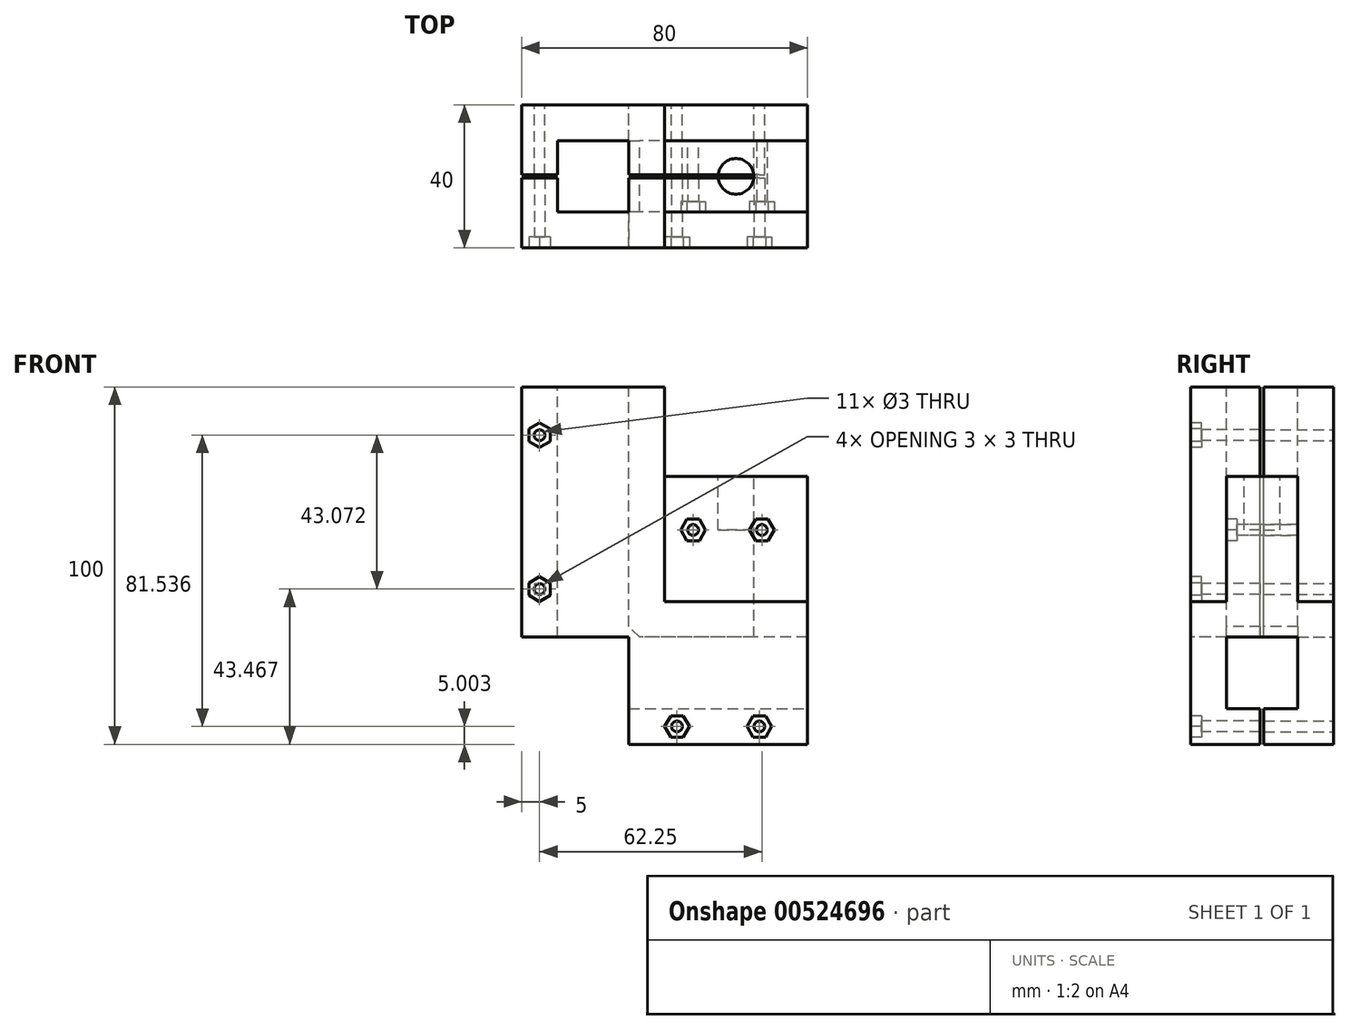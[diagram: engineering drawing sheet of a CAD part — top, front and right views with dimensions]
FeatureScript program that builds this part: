
annotation { "Feature Type Name" : "Feature", "Feature Type Description" : "" }
export const myFeature = defineFeature(function(context is Context, id is Id, definition is map)
    precondition{}
    {
        {
            var Q0;
            Q0=qCreatedBy(makeId("Front.planeOp"),FACE);
            var sketch = newSketch(context, id + "F0", { "sketchPlane" : qUnion([Q0])});
            skLineSegment(sketch, "E0", {"start": v(-50, 89.2) * mm, "end": v(-50, 19.2) * mm});
            skLineSegment(sketch, "E1", {"start": v(-50, 19.2) * mm, "end": v(0, 19.2) * mm});
            skLineSegment(sketch, "E2", {"start": v(0, 19.2) * mm, "end": v(0, 64.2) * mm});
            skLineSegment(sketch, "E3", {"start": v(0, 64.2) * mm, "end": v(-40, 64.2) * mm});
            skLineSegment(sketch, "E4", {"start": v(-40, 64.2) * mm, "end": v(-40, 89.2) * mm});
            skLineSegment(sketch, "E5", {"start": v(-40, 89.2) * mm, "end": v(-50, 89.2) * mm});
            skSolve(sketch);
        }
        {
            var Q0;
            Q0=qSketchRegion(id+"F0",true);
            extrude(context, id + "F1", {"entities" : qUnion([Q0]), "depth" : 20 * mm, "offsetDistance" : 25 * mm});
        }
        {
            var Q0;
            Q0=makeQuery(id+"F1.opExtrude","CAP_FACE",FACE,{"disambiguationData":[OSD([sQuery(id+"F0.wireOp",EDGE,"E0"),sQuery(id+"F0.wireOp",EDGE,"E1"),sQuery(id+"F0.wireOp",EDGE,"E2"),sQuery(id+"F0.wireOp",EDGE,"E3"),sQuery(id+"F0.wireOp",EDGE,"E4"),sQuery(id+"F0.wireOp",EDGE,"E5")])],"isStart":false});
            var sketch = newSketch(context, id + "F2", { "sketchPlane" : qUnion([Q0])});
            skLineSegment(sketch, "E6", {"start": v(-50, 29.2) * mm, "end": v(0, 29.2) * mm});
            skSolve(sketch);
        }
        {
            var Q0;
            {var subQ0=sQuery(id+"F2.wireOp",EDGE,"E6");Q0=makeQuery(id+"F2.imprint","IMPRINT",FACE,{"disambiguationData":[TD([[makeQuery(id+"F2.imprint","IMPRINT",EDGE,{"derivedFrom":subQ0}),-1.0]])]});}
            extrude(context, id + "F3", {"entities" : qUnion([Q0]), "operationType" : NewBodyOperationType.ADD, "depth" : 10 * mm, "offsetDistance" : 25 * mm});
        }
        {
            var Q0;
            Q0=makeQuery(id+"F1.opExtrude","CAP_FACE",FACE,{"disambiguationData":[OSD([sQuery(id+"F0.wireOp",EDGE,"E0"),sQuery(id+"F0.wireOp",EDGE,"E1"),sQuery(id+"F0.wireOp",EDGE,"E2"),sQuery(id+"F0.wireOp",EDGE,"E3"),sQuery(id+"F0.wireOp",EDGE,"E4"),sQuery(id+"F0.wireOp",EDGE,"E5")])],"isStart":true});
            var sketch = newSketch(context, id + "F4", { "sketchPlane" : qUnion([Q0])});
            skLineSegment(sketch, "E7", {"start": v(0, 29.2) * mm, "end": v(50, 29.2) * mm});
            skSolve(sketch);
        }
        {
            var Q0;
            {var subQ0=sQuery(id+"F4.wireOp",EDGE,"E7");Q0=makeQuery(id+"F4.imprint","IMPRINT",FACE,{"disambiguationData":[TD([[makeQuery(id+"F4.imprint","IMPRINT",EDGE,{"derivedFrom":subQ0}),-1.0]])]});}
            extrude(context, id + "F5", {"entities" : qUnion([Q0]), "operationType" : NewBodyOperationType.ADD, "depth" : 10 * mm, "offsetDistance" : 25 * mm});
        }
        {
            var Q0;
            {var subQ0=sQuery(id+"F0.wireOp",EDGE,"E1");Q0=makeQuery(id+"F5.boolean.opBoolean","MERGE",FACE,{"derivedFrom":[makeQuery(id+"F3.boolean.opBoolean","MERGE",FACE,{"derivedFrom":[makeQuery(id+"F1.opExtrude","SWEPT_FACE",FACE,{"disambiguationData":[OSD([subQ0])]}),makeQuery(id+"F3.opExtrude","SWEPT_FACE",FACE,{"disambiguationData":[OSD([subQ0])]})]}),makeQuery(id+"F5.opExtrude","SWEPT_FACE",FACE,{"disambiguationData":[OSD([subQ0])]})]});}
            var sketch = newSketch(context, id + "F6", { "sketchPlane" : qUnion([Q0])});
            skLineSegment(sketch, "E8", {"start": v(0, 20) * mm, "end": v(-50, 20) * mm});
            skLineSegment(sketch, "E9", {"start": v(0, 0) * mm, "end": v(-50, 0) * mm});
            skSolve(sketch);
        }
        {
            var Q0;
            {var subQ0=sQuery(id+"F6.wireOp",EDGE,"E8");Q0=makeQuery(id+"F6.imprint","IMPRINT",FACE,{"disambiguationData":[TD([[makeQuery(id+"F6.imprint","IMPRINT",EDGE,{"derivedFrom":subQ0}),-1.0]])]});}
            var Q1;
            {var subQ0=sQuery(id+"F6.wireOp",EDGE,"E9");Q1=makeQuery(id+"F6.imprint","IMPRINT",FACE,{"disambiguationData":[TD([[makeQuery(id+"F6.imprint","IMPRINT",EDGE,{"derivedFrom":subQ0}),1.0]])]});}
            extrude(context, id + "F7", {"entities" : qUnion([Q0, Q1]), "operationType" : NewBodyOperationType.ADD, "depth" : 30 * mm, "offsetDistance" : 25 * mm});
        }
        {
            var Q0;
            Q0=makeQuery(id+"F5.opExtrude","SWEPT_FACE",FACE,{"disambiguationData":[OSD([sQuery(id+"F4.wireOp",EDGE,"E7")])]});
            var sketch = newSketch(context, id + "F8", { "sketchPlane" : qUnion([Q0])});
            skLineSegment(sketch, "E10", {"start": v(-30, -25) * mm, "end": v(-28.27, -28) * mm});
            skLineSegment(sketch, "E11", {"start": v(-28.27, -28) * mm, "end": v(-24.8, -28) * mm});
            skLineSegment(sketch, "E12", {"start": v(-24.8, -28) * mm, "end": v(-23.07, -25) * mm});
            skLineSegment(sketch, "E13", {"start": v(-23.07, -25) * mm, "end": v(-24.8, -22) * mm});
            skLineSegment(sketch, "E14", {"start": v(-24.8, -22) * mm, "end": v(-28.27, -22) * mm});
            skLineSegment(sketch, "E15", {"start": v(-28.27, -22) * mm, "end": v(-30, -25) * mm});
            skCircle(sketch, "E16", {"center": v(-26.54, -25) * mm, "radius": 1.5 * mm});
            skLineSegment(sketch, "E17", {"start": v(-16.93, -25) * mm, "end": v(-15.2, -28) * mm});
            skLineSegment(sketch, "E18", {"start": v(-15.2, -28) * mm, "end": v(-11.73, -28) * mm});
            skLineSegment(sketch, "E19", {"start": v(-11.73, -28) * mm, "end": v(-10, -25) * mm});
            skLineSegment(sketch, "E20", {"start": v(-10, -25) * mm, "end": v(-11.73, -22) * mm});
            skLineSegment(sketch, "E21", {"start": v(-11.73, -22) * mm, "end": v(-15.2, -22) * mm});
            skLineSegment(sketch, "E22", {"start": v(-15.2, -22) * mm, "end": v(-16.93, -25) * mm});
            skCircle(sketch, "E23", {"center": v(-13.46, -25) * mm, "radius": 1.5 * mm});
            skLineSegment(sketch, "E24", {"start": v(-70, 5) * mm, "end": v(-68.27, 2) * mm});
            skLineSegment(sketch, "E25", {"start": v(-68.27, 2) * mm, "end": v(-64.8, 2) * mm});
            skLineSegment(sketch, "E26", {"start": v(-64.8, 2) * mm, "end": v(-63.07, 5) * mm});
            skLineSegment(sketch, "E27", {"start": v(-63.07, 5) * mm, "end": v(-64.8, 8) * mm});
            skLineSegment(sketch, "E28", {"start": v(-64.8, 8) * mm, "end": v(-68.27, 8) * mm});
            skLineSegment(sketch, "E29", {"start": v(-68.27, 8) * mm, "end": v(-70, 5) * mm});
            skCircle(sketch, "E30", {"center": v(-66.54, 5) * mm, "radius": 1.5 * mm});
            skLineSegment(sketch, "E31", {"start": v(-16.93, 5) * mm, "end": v(-15.2, 2) * mm});
            skLineSegment(sketch, "E32", {"start": v(-15.2, 2) * mm, "end": v(-11.73, 2) * mm});
            skLineSegment(sketch, "E33", {"start": v(-11.73, 2) * mm, "end": v(-10, 5) * mm});
            skLineSegment(sketch, "E34", {"start": v(-10, 5) * mm, "end": v(-11.73, 8) * mm});
            skLineSegment(sketch, "E35", {"start": v(-11.73, 8) * mm, "end": v(-15.2, 8) * mm});
            skLineSegment(sketch, "E36", {"start": v(-15.2, 8) * mm, "end": v(-16.93, 5) * mm});
            skCircle(sketch, "E37", {"center": v(-13.46, 5) * mm, "radius": 1.5 * mm});
            skLineSegment(sketch, "E38", {"start": v(-40, 0) * mm, "end": v(-40, 10) * mm});
            skLineSegment(sketch, "E39.bottom", {"start": v(-40, -20) * mm, "end": v(-50, -20) * mm});
            skLineSegment(sketch, "E39.top", {"start": v(-40, -30) * mm, "end": v(-50, -30) * mm});
            skLineSegment(sketch, "E39.left", {"start": v(-40, -20) * mm, "end": v(-40, -30) * mm});
            skLineSegment(sketch, "E39.right", {"start": v(-50, -20) * mm, "end": v(-50, -30) * mm});
            skSolve(sketch);
        }
        {
            var Q0;
            {var subQ0=sQuery(id+"F8.wireOp",EDGE,"E38");Q0=makeQuery(id+"F8.imprint","IMPRINT",FACE,{"disambiguationData":[TD([[makeQuery(id+"F8.imprint","IMPRINT",EDGE,{"derivedFrom":subQ0}),1.0]])]});}
            var Q1;
            Q1=makeQuery(id+"F8.imprint","IMPRINT",FACE,{"disambiguationData":[TD([[makeQuery(id+"F8.imprint","IMPRINT",EDGE,{"derivedFrom":sQuery(id+"F8.wireOp",EDGE,"E39.bottom")}),1.0]])]});
            extrude(context, id + "F9", {"entities" : qUnion([Q0, Q1]), "operationType" : NewBodyOperationType.ADD, "depth" : 60 * mm, "offsetDistance" : 25 * mm});
        }
        {
            var Q0;
            {var subQ0=sQuery(id+"F0.wireOp",EDGE,"E0");var subQ1=sQuery(id+"F0.wireOp",EDGE,"E1");var subQ2=makeQuery(id+"F5.boolean.opBoolean","MERGE",EDGE,{"derivedFrom":[makeQuery(id+"F3.boolean.opBoolean","MERGE",EDGE,{"derivedFrom":[makeQuery(id+"F1.opExtrude","SWEPT_EDGE",EDGE,{"disambiguationData":[OSD([subQ0,subQ1])]}),makeQuery(id+"F3.opExtrude","SWEPT_EDGE",EDGE,{"disambiguationData":[OSD([subQ0,subQ1])]})]}),makeQuery(id+"F5.opExtrude","SWEPT_EDGE",EDGE,{"disambiguationData":[OSD([subQ0,subQ1])]})]});Q0=makeQuery(id+"F9.boolean.opBoolean","MERGE",FACE,{"derivedFrom":[makeQuery(id+"F7.boolean.opBoolean","MERGE",FACE,{"derivedFrom":[makeQuery(id+"F5.boolean.opBoolean","MERGE",FACE,{"derivedFrom":[makeQuery(id+"F3.boolean.opBoolean","MERGE",FACE,{"derivedFrom":[makeQuery(id+"F1.opExtrude","SWEPT_FACE",FACE,{"disambiguationData":[OSD([subQ0])]}),makeQuery(id+"F3.opExtrude","SWEPT_FACE",FACE,{"disambiguationData":[OSD([subQ0])]})]}),makeQuery(id+"F5.opExtrude","SWEPT_FACE",FACE,{"disambiguationData":[OSD([subQ0])]})]}),makeQuery(id+"F7.opExtrude","SWEPT_FACE",FACE,{"disambiguationData":[OSD([subQ0,subQ1]),TDD([makeQuery(id+"F6.imprint","IMPRINT",EDGE,{"disambiguationData":[TD([[makeQuery(id+"F6.imprint","INTERSECT",VERTEX,{"derivedFrom":[makeQuery(id+"F3.opExtrude","CAP_EDGE",EDGE,{"disambiguationData":[OSD([subQ1])],"isStart":false}),subQ2]}),-1.0]])],"derivedFrom":subQ2})])]}),makeQuery(id+"F7.opExtrude","SWEPT_FACE",FACE,{"disambiguationData":[OSD([subQ0,subQ1]),TDD([makeQuery(id+"F6.imprint","IMPRINT",EDGE,{"disambiguationData":[TD([[makeQuery(id+"F6.imprint","INTERSECT",VERTEX,{"derivedFrom":[makeQuery(id+"F5.opExtrude","CAP_EDGE",EDGE,{"disambiguationData":[OSD([subQ1])],"isStart":false}),subQ2]}),1.0]])],"derivedFrom":subQ2})])]})]}),makeQuery(id+"F9.opExtrude","SWEPT_FACE",FACE,{"disambiguationData":[OSD([sQuery(id+"F8.wireOp",EDGE,"E39.right")])]}),makeQuery(id+"F9.opExtrude","SWEPT_FACE",FACE,{"disambiguationData":[OSD([subQ0,sQuery(id+"F4.wireOp",EDGE,"E7")])]})]});}
            var sketch = newSketch(context, id + "F10", { "sketchPlane" : qUnion([Q0])});
            skLineSegment(sketch, "E40", {"start": v(20, 19.2) * mm, "end": v(20, 89.2) * mm});
            skLineSegment(sketch, "E41", {"start": v(0, 19.2) * mm, "end": v(0, 89.2) * mm});
            skLineSegment(sketch, "E42", {"start": v(20, 19.2) * mm, "end": v(30, 19.2) * mm});
            skLineSegment(sketch, "E43", {"start": v(0, 19.2) * mm, "end": v(-10, 19.2) * mm});
            skSolve(sketch);
        }
        {
            var Q0;
            {var subQ0=sQuery(id+"F10.wireOp",EDGE,"E40");Q0=makeQuery(id+"F10.imprint","IMPRINT",FACE,{"disambiguationData":[TD([[makeQuery(id+"F10.imprint","IMPRINT",EDGE,{"derivedFrom":subQ0}),-1.0]])]});}
            var Q1;
            {var subQ0=sQuery(id+"F10.wireOp",EDGE,"E41");Q1=makeQuery(id+"F10.imprint","IMPRINT",FACE,{"disambiguationData":[TD([[makeQuery(id+"F10.imprint","IMPRINT",EDGE,{"derivedFrom":subQ0}),1.0]])]});}
            extrude(context, id + "F11", {"entities" : qUnion([Q0, Q1]), "operationType" : NewBodyOperationType.ADD, "depth" : 30 * mm, "offsetDistance" : 25 * mm});
        }
        {
            var Q0;
            Q0=makeQuery(id+"F1.opExtrude","SWEPT_FACE",FACE,{"disambiguationData":[OSD([sQuery(id+"F0.wireOp",EDGE,"E3")])]});
            var sketch = newSketch(context, id + "F12", { "sketchPlane" : qUnion([Q0])});
            skCircle(sketch, "E44", {"center": v(-20, -10) * mm, "radius": 5 * mm});
            skSolve(sketch);
        }
        {
            var Q0;
            Q0=makeQuery(id+"F12.imprint","IMPRINT",FACE,{"disambiguationData":[TD([[makeQuery(id+"F12.imprint","IMPRINT",EDGE,{"derivedFrom":sQuery(id+"F12.wireOp",EDGE,"E44")}),1.0]])]});
            extrude(context, id + "F13", {"entities" : qUnion([Q0]), "operationType" : NewBodyOperationType.REMOVE, "oppositeDirection" : true, "depth" : 15 * mm, "offsetDistance" : 25 * mm});
        }
        {
            var Q0;
            {var subQ0=sQuery(id+"F8.wireOp",EDGE,"E39.right");var subQ1=sQuery(id+"F8.wireOp",EDGE,"E39.top");var subQ3=sQuery(id+"F0.wireOp",EDGE,"E0");var subQ5=sQuery(id+"F4.wireOp",EDGE,"E7");var subQ6=sQuery(id+"F0.wireOp",EDGE,"E5");var subQ7=makeQuery(id+"F9.boolean.opBoolean","MERGE",EDGE,{"derivedFrom":[makeQuery(id+"F1.opExtrude","SWEPT_EDGE",EDGE,{"disambiguationData":[OSD([subQ3,subQ6])]}),makeQuery(id+"F9.opExtrude","CAP_EDGE",EDGE,{"disambiguationData":[OSD([subQ0])],"isStart":false}),makeQuery(id+"F9.opExtrude","CAP_EDGE",EDGE,{"disambiguationData":[OSD([subQ3,subQ5])],"isStart":false})]});Q0=makeQuery(id+"F11.boolean.opBoolean","MERGE",FACE,{"derivedFrom":[makeQuery(id+"F9.boolean.opBoolean","MERGE",FACE,{"derivedFrom":[makeQuery(id+"F1.opExtrude","SWEPT_FACE",FACE,{"disambiguationData":[OSD([subQ6])]}),makeQuery(id+"F9.opExtrude","CAP_FACE",FACE,{"disambiguationData":[OSD([subQ3,subQ5,sQuery(id+"F8.wireOp",EDGE,"E38")])],"isStart":false}),makeQuery(id+"F9.opExtrude","CAP_FACE",FACE,{"disambiguationData":[OSD([sQuery(id+"F8.wireOp",EDGE,"E39.bottom"),subQ1,sQuery(id+"F8.wireOp",EDGE,"E39.left"),subQ0])],"isStart":false})]}),makeQuery(id+"F11.opExtrude","SWEPT_FACE",FACE,{"disambiguationData":[OSD([subQ3,subQ6,subQ5,subQ0]),TDD([makeQuery(id+"F10.imprint","IMPRINT",EDGE,{"disambiguationData":[TD([[makeQuery(id+"F10.imprint","INTERSECT",VERTEX,{"derivedFrom":[subQ7,sQuery(id+"F10.wireOp",EDGE,"E41")]}),-1.0]])],"derivedFrom":subQ7})])]}),makeQuery(id+"F11.opExtrude","SWEPT_FACE",FACE,{"disambiguationData":[OSD([subQ3,subQ6,subQ5,subQ0]),TDD([makeQuery(id+"F10.imprint","IMPRINT",EDGE,{"disambiguationData":[TD([[makeQuery(id+"F10.imprint","INTERSECT",VERTEX,{"derivedFrom":[subQ7,sQuery(id+"F10.wireOp",EDGE,"E40")]}),1.0]])],"derivedFrom":subQ7})])]})]});}
            var sketch = newSketch(context, id + "F14", { "sketchPlane" : qUnion([Q0])});
            skLineSegment(sketch, "E45", {"start": v(-40, -10) * mm, "end": v(-40, -9.5) * mm});
            skLineSegment(sketch, "E46", {"start": v(-40, -10) * mm, "end": v(-40, -10.5) * mm});
            skLineSegment(sketch, "E47", {"start": v(-40, -10.5) * mm, "end": v(-50, -10.5) * mm});
            skLineSegment(sketch, "E48", {"start": v(-40, -9.5) * mm, "end": v(-50, -9.5) * mm});
            skSolve(sketch);
        }
        {
            var Q0;
            Q0=makeQuery(id+"F1.opExtrude","SWEPT_FACE",FACE,{"disambiguationData":[OSD([sQuery(id+"F0.wireOp",EDGE,"E3")])]});
            var sketch = newSketch(context, id + "F15", { "sketchPlane" : qUnion([Q0])});
            skLineSegment(sketch, "E49", {"start": v(-40, 54.2) * mm, "end": v(-40, -10.5) * mm});
            skLineSegment(sketch, "E50", {"start": v(-40, -10.5) * mm, "end": v(0, -10.5) * mm});
            skLineSegment(sketch, "E51", {"start": v(-40, -9.5) * mm, "end": v(0, -9.5) * mm});
            skSolve(sketch);
        }
        {
            var Q0;
            {var subQ0=sQuery(id+"F15.wireOp",EDGE,"E50");var subQ3=makeQuery(id+"F13.boolean.opBoolean","COPY",EDGE,{"derivedFrom":makeQuery(id+"F13.opExtrude","CAP_EDGE",EDGE,{"disambiguationData":[OSD([sQuery(id+"F12.wireOp",EDGE,"E44")])],"isStart":true})});var subQ4=makeQuery(id+"F15.imprint","INTERSECT",VERTEX,{"disambiguationData":[OD(1.0)],"derivedFrom":[subQ3,subQ0]});Q0=makeQuery(id+"F15.imprint","IMPRINT",FACE,{"disambiguationData":[TD([[makeQuery(id+"F15.imprint","IMPRINT",EDGE,{"disambiguationData":[TD([[subQ4,-1.0]])],"derivedFrom":subQ3}),-1.0]])]});}
            var Q1;
            Q1=makeQuery(id+"F14.imprint","IMPRINT",FACE,{"disambiguationData":[TD([[makeQuery(id+"F14.imprint","IMPRINT",EDGE,{"derivedFrom":sQuery(id+"F14.wireOp",EDGE,"E45")}),1.0]])]});
            var Q2;
            {var subQ0=sQuery(id+"F15.wireOp",EDGE,"E50");var subQ1=makeQuery(id+"F13.boolean.opBoolean","COPY",EDGE,{"derivedFrom":makeQuery(id+"F13.opExtrude","CAP_EDGE",EDGE,{"disambiguationData":[OSD([sQuery(id+"F12.wireOp",EDGE,"E44")])],"isStart":true})});var subQ2=makeQuery(id+"F15.imprint","INTERSECT",VERTEX,{"disambiguationData":[OD(0.0)],"derivedFrom":[subQ1,subQ0]});Q2=makeQuery(id+"F15.imprint","IMPRINT",FACE,{"disambiguationData":[TD([[makeQuery(id+"F15.imprint","IMPRINT",EDGE,{"disambiguationData":[TD([[subQ2,-1.0]])],"derivedFrom":subQ0}),1.0]])]});}
            var Q3;
            {var subQ1=sQuery(id+"F15.wireOp",EDGE,"E49");var subQ3=sQuery(id+"F15.wireOp",EDGE,"E51");var subQ4=makeQuery(id+"F15.imprint","INTERSECT",VERTEX,{"derivedFrom":[subQ1,subQ3]});Q3=makeQuery(id+"F15.imprint","IMPRINT",FACE,{"disambiguationData":[TD([[makeQuery(id+"F15.imprint","IMPRINT",EDGE,{"disambiguationData":[TD([[subQ4,-1.0]])],"derivedFrom":subQ3}),-1.0]])]});}
            extrude(context, id + "F16", {"entities" : qUnion([Q0, Q1, Q2, Q3]), "operationType" : NewBodyOperationType.REMOVE, "oppositeDirection" : true, "depth" : 70 * mm, "offsetDistance" : 25 * mm});
        }
        {
            var Q0;
            {var subQ0=sQuery(id+"F0.wireOp",EDGE,"E1");var subQ1=sQuery(id+"F0.wireOp",EDGE,"E0");var subQ2=makeQuery(id+"F5.boolean.opBoolean","MERGE",EDGE,{"derivedFrom":[makeQuery(id+"F3.boolean.opBoolean","MERGE",EDGE,{"derivedFrom":[makeQuery(id+"F1.opExtrude","SWEPT_EDGE",EDGE,{"disambiguationData":[OSD([subQ1,subQ0])]}),makeQuery(id+"F3.opExtrude","SWEPT_EDGE",EDGE,{"disambiguationData":[OSD([subQ1,subQ0])]})]}),makeQuery(id+"F5.opExtrude","SWEPT_EDGE",EDGE,{"disambiguationData":[OSD([subQ1,subQ0])]})]});var subQ3=sQuery(id+"F6.wireOp",EDGE,"E9");Q0=makeQuery(id+"F16.boolean.opBoolean","SPLIT",EDGE,{"disambiguationData":[TD([makeQuery(id+"F7.opExtrude","SWEPT_FACE",FACE,{"disambiguationData":[OSD([subQ3])]})])],"derivedFrom":subQ2});}
            var Q1;
            {var subQ0=sQuery(id+"F0.wireOp",EDGE,"E1");var subQ1=sQuery(id+"F0.wireOp",EDGE,"E0");var subQ2=makeQuery(id+"F5.boolean.opBoolean","MERGE",EDGE,{"derivedFrom":[makeQuery(id+"F3.boolean.opBoolean","MERGE",EDGE,{"derivedFrom":[makeQuery(id+"F1.opExtrude","SWEPT_EDGE",EDGE,{"disambiguationData":[OSD([subQ1,subQ0])]}),makeQuery(id+"F3.opExtrude","SWEPT_EDGE",EDGE,{"disambiguationData":[OSD([subQ1,subQ0])]})]}),makeQuery(id+"F5.opExtrude","SWEPT_EDGE",EDGE,{"disambiguationData":[OSD([subQ1,subQ0])]})]});var subQ3=sQuery(id+"F6.wireOp",EDGE,"E8");Q1=makeQuery(id+"F16.boolean.opBoolean","SPLIT",EDGE,{"disambiguationData":[TD([makeQuery(id+"F7.opExtrude","SWEPT_FACE",FACE,{"disambiguationData":[OSD([subQ3])]})])],"derivedFrom":subQ2});}
            chamfer(context, id + "F17", {"entities" : qUnion([Q0, Q1]), "width" : 3 * mm, "tangentPropagation" : true});
        }
        {
            var Q0;
            Q0=makeQuery(id+"F17.opChamfer","MERGE",FACE,{"derivedFrom":[makeQuery(id+"F7.opExtrude","SWEPT_FACE",FACE,{"disambiguationData":[OSD([sQuery(id+"F6.wireOp",EDGE,"E9")])]}),makeQuery(id+"F11.opExtrude","SWEPT_FACE",FACE,{"disambiguationData":[OSD([sQuery(id+"F10.wireOp",EDGE,"E41")])]})]});
            var sketch = newSketch(context, id + "F18", { "sketchPlane" : qUnion([Q0])});
            skLineSegment(sketch, "E52", {"start": v(-80, 19.2) * mm, "end": v(-70, 19.2) * mm});
            skLineSegment(sketch, "E53", {"start": v(-70, 19.2) * mm, "end": v(-70, 89.2) * mm});
            skLineSegment(sketch, "E54", {"start": v(-50, -10.8) * mm, "end": v(-50, -0.8) * mm});
            skLineSegment(sketch, "E55", {"start": v(-50, -0.8) * mm, "end": v(0, -0.8) * mm});
            skSolve(sketch);
        }
        {
            var Q0;
            Q0=makeQuery(id+"F17.opChamfer","MERGE",FACE,{"derivedFrom":[makeQuery(id+"F7.opExtrude","SWEPT_FACE",FACE,{"disambiguationData":[OSD([sQuery(id+"F6.wireOp",EDGE,"E8")])]}),makeQuery(id+"F11.opExtrude","SWEPT_FACE",FACE,{"disambiguationData":[OSD([sQuery(id+"F10.wireOp",EDGE,"E40")])]})]});
            var sketch = newSketch(context, id + "F19", { "sketchPlane" : qUnion([Q0])});
            skLineSegment(sketch, "E56", {"start": v(80, 19.2) * mm, "end": v(70, 19.2) * mm});
            skLineSegment(sketch, "E57", {"start": v(70, 19.2) * mm, "end": v(70, 89.2) * mm});
            skLineSegment(sketch, "E58", {"start": v(50, -10.8) * mm, "end": v(50, -0.8) * mm});
            skLineSegment(sketch, "E59", {"start": v(50, -0.8) * mm, "end": v(0, -0.8) * mm});
            skSolve(sketch);
        }
        {
            var Q0;
            Q0=makeQuery(id+"F18.imprint","IMPRINT",FACE,{"disambiguationData":[TD([[makeQuery(id+"F18.imprint","IMPRINT",EDGE,{"derivedFrom":sQuery(id+"F18.wireOp",EDGE,"E52")}),1.0]])]});
            var Q1;
            Q1=makeQuery(id+"F18.imprint","IMPRINT",FACE,{"disambiguationData":[TD([[makeQuery(id+"F18.imprint","IMPRINT",EDGE,{"derivedFrom":sQuery(id+"F18.wireOp",EDGE,"E54")}),-1.0]])]});
            extrude(context, id + "F20", {"entities" : qUnion([Q0, Q1]), "operationType" : NewBodyOperationType.ADD, "depth" : 9.5 * mm, "offsetDistance" : 25 * mm});
        }
        {
            var Q0;
            Q0=makeQuery(id+"F19.imprint","IMPRINT",FACE,{"disambiguationData":[TD([[makeQuery(id+"F19.imprint","IMPRINT",EDGE,{"derivedFrom":sQuery(id+"F19.wireOp",EDGE,"E56")}),-1.0]])]});
            var Q1;
            Q1=makeQuery(id+"F19.imprint","IMPRINT",FACE,{"disambiguationData":[TD([[makeQuery(id+"F19.imprint","IMPRINT",EDGE,{"derivedFrom":sQuery(id+"F19.wireOp",EDGE,"E58")}),1.0]])]});
            extrude(context, id + "F21", {"entities" : qUnion([Q0, Q1]), "operationType" : NewBodyOperationType.ADD, "depth" : 9.5 * mm, "offsetDistance" : 25 * mm});
        }
        {
            var Q0;
            {var subQ0=sQuery(id+"F8.wireOp",EDGE,"E39.top");var subQ1=sQuery(id+"F0.wireOp",EDGE,"E1");var subQ2=sQuery(id+"F0.wireOp",EDGE,"E0");Q0=makeQuery(id+"F11.boolean.opBoolean","MERGE",FACE,{"derivedFrom":[makeQuery(id+"F9.boolean.opBoolean","MERGE",FACE,{"derivedFrom":[makeQuery(id+"F7.boolean.opBoolean","MERGE",FACE,{"derivedFrom":[makeQuery(id+"F3.opExtrude","CAP_FACE",FACE,{"disambiguationData":[OSD([subQ2,subQ1,sQuery(id+"F0.wireOp",EDGE,"E2"),sQuery(id+"F2.wireOp",EDGE,"E6")])],"isStart":false}),makeQuery(id+"F7.opExtrude","SWEPT_FACE",FACE,{"disambiguationData":[OSD([subQ1]),TDD([makeQuery(id+"F6.imprint","IMPRINT",EDGE,{"derivedFrom":makeQuery(id+"F3.opExtrude","CAP_EDGE",EDGE,{"disambiguationData":[OSD([subQ1])],"isStart":false})})])]})]}),makeQuery(id+"F9.opExtrude","SWEPT_FACE",FACE,{"disambiguationData":[OSD([subQ0])]})]}),makeQuery(id+"F11.opExtrude","SWEPT_FACE",FACE,{"disambiguationData":[OSD([subQ2,subQ1,subQ0,sQuery(id+"F8.wireOp",EDGE,"E39.right")])]})]});}
            var sketch = newSketch(context, id + "F22", { "sketchPlane" : qUnion([Q0])});
            skLineSegment(sketch, "E60", {"start": v(-75, 79.2) * mm, "end": v(-78, 77.46) * mm});
            skLineSegment(sketch, "E61", {"start": v(-78, 77.46) * mm, "end": v(-78, 74) * mm});
            skLineSegment(sketch, "E62", {"start": v(-78, 74) * mm, "end": v(-75, 72.26) * mm});
            skLineSegment(sketch, "E63", {"start": v(-75, 72.26) * mm, "end": v(-72, 74) * mm});
            skLineSegment(sketch, "E64", {"start": v(-72, 74) * mm, "end": v(-72, 77.46) * mm});
            skLineSegment(sketch, "E65", {"start": v(-72, 77.46) * mm, "end": v(-75, 79.2) * mm});
            skCircle(sketch, "E66", {"center": v(-75, 75.73) * mm, "radius": 1.5 * mm});
            skLineSegment(sketch, "E67", {"start": v(-75, 36.12) * mm, "end": v(-78, 34.39) * mm});
            skLineSegment(sketch, "E68", {"start": v(-78, 34.39) * mm, "end": v(-78, 30.93) * mm});
            skLineSegment(sketch, "E69", {"start": v(-78, 30.93) * mm, "end": v(-75, 29.2) * mm});
            skLineSegment(sketch, "E70", {"start": v(-75, 29.2) * mm, "end": v(-72, 30.93) * mm});
            skLineSegment(sketch, "E71", {"start": v(-72, 30.93) * mm, "end": v(-72, 34.39) * mm});
            skLineSegment(sketch, "E72", {"start": v(-72, 34.39) * mm, "end": v(-75, 36.12) * mm});
            skCircle(sketch, "E73", {"center": v(-75, 32.66) * mm, "radius": 1.5 * mm});
            skLineSegment(sketch, "E74", {"start": v(-40, -5.8) * mm, "end": v(-38.27, -8.8) * mm});
            skLineSegment(sketch, "E75", {"start": v(-38.27, -8.8) * mm, "end": v(-34.8, -8.8) * mm});
            skLineSegment(sketch, "E76", {"start": v(-34.8, -8.8) * mm, "end": v(-33.07, -5.8) * mm});
            skLineSegment(sketch, "E77", {"start": v(-33.07, -5.8) * mm, "end": v(-34.8, -2.8) * mm});
            skLineSegment(sketch, "E78", {"start": v(-34.8, -2.8) * mm, "end": v(-38.27, -2.8) * mm});
            skLineSegment(sketch, "E79", {"start": v(-38.27, -2.8) * mm, "end": v(-40, -5.8) * mm});
            skCircle(sketch, "E80", {"center": v(-36.54, -5.8) * mm, "radius": 1.5 * mm});
            skLineSegment(sketch, "E81", {"start": v(-16.93, -5.8) * mm, "end": v(-15.2, -8.8) * mm});
            skLineSegment(sketch, "E82", {"start": v(-15.2, -8.8) * mm, "end": v(-11.73, -8.8) * mm});
            skLineSegment(sketch, "E83", {"start": v(-11.73, -8.8) * mm, "end": v(-10, -5.8) * mm});
            skLineSegment(sketch, "E84", {"start": v(-10, -5.8) * mm, "end": v(-11.73, -2.8) * mm});
            skLineSegment(sketch, "E85", {"start": v(-11.73, -2.8) * mm, "end": v(-15.2, -2.8) * mm});
            skLineSegment(sketch, "E86", {"start": v(-15.2, -2.8) * mm, "end": v(-16.93, -5.8) * mm});
            skCircle(sketch, "E87", {"center": v(-13.46, -5.8) * mm, "radius": 1.5 * mm});
            skSolve(sketch);
        }
        {
            var Q0;
            Q0=makeQuery(id+"F22.imprint","IMPRINT",FACE,{"disambiguationData":[TD([[makeQuery(id+"F22.imprint","IMPRINT",EDGE,{"derivedFrom":sQuery(id+"F22.wireOp",EDGE,"E60")}),1.0]])]});
            var Q1;
            Q1=makeQuery(id+"F22.imprint","IMPRINT",FACE,{"disambiguationData":[TD([[makeQuery(id+"F22.imprint","IMPRINT",EDGE,{"derivedFrom":sQuery(id+"F22.wireOp",EDGE,"E67")}),1.0]])]});
            var Q2;
            Q2=makeQuery(id+"F22.imprint","IMPRINT",FACE,{"disambiguationData":[TD([[makeQuery(id+"F22.imprint","IMPRINT",EDGE,{"derivedFrom":sQuery(id+"F22.wireOp",EDGE,"E74")}),1.0]])]});
            var Q3;
            Q3=makeQuery(id+"F22.imprint","IMPRINT",FACE,{"disambiguationData":[TD([[makeQuery(id+"F22.imprint","IMPRINT",EDGE,{"derivedFrom":sQuery(id+"F22.wireOp",EDGE,"E81")}),1.0]])]});
            extrude(context, id + "F23", {"entities" : qUnion([Q0, Q1, Q2, Q3]), "operationType" : NewBodyOperationType.REMOVE, "oppositeDirection" : true, "depth" : 3 * mm, "offsetDistance" : 25 * mm});
        }
        {
            var Q0;
            {var subQ0=sQuery(id+"F8.wireOp",EDGE,"E39.top");var subQ1=sQuery(id+"F0.wireOp",EDGE,"E1");var subQ2=sQuery(id+"F0.wireOp",EDGE,"E0");Q0=makeQuery(id+"F23.boolean.opBoolean","SPLIT",FACE,{"disambiguationData":[TD([makeQuery(id+"F23.opExtrude","SWEPT_FACE",FACE,{"disambiguationData":[OSD([sQuery(id+"F22.wireOp",EDGE,"E66")])]})])],"derivedFrom":makeQuery(id+"F11.boolean.opBoolean","MERGE",FACE,{"derivedFrom":[makeQuery(id+"F9.boolean.opBoolean","MERGE",FACE,{"derivedFrom":[makeQuery(id+"F7.boolean.opBoolean","MERGE",FACE,{"derivedFrom":[makeQuery(id+"F3.opExtrude","CAP_FACE",FACE,{"disambiguationData":[OSD([subQ2,subQ1,sQuery(id+"F0.wireOp",EDGE,"E2"),sQuery(id+"F2.wireOp",EDGE,"E6")])],"isStart":false}),makeQuery(id+"F7.opExtrude","SWEPT_FACE",FACE,{"disambiguationData":[OSD([subQ1]),TDD([makeQuery(id+"F6.imprint","IMPRINT",EDGE,{"derivedFrom":makeQuery(id+"F3.opExtrude","CAP_EDGE",EDGE,{"disambiguationData":[OSD([subQ1])],"isStart":false})})])]})]}),makeQuery(id+"F9.opExtrude","SWEPT_FACE",FACE,{"disambiguationData":[OSD([subQ0])]})]}),makeQuery(id+"F11.opExtrude","SWEPT_FACE",FACE,{"disambiguationData":[OSD([subQ2,subQ1,subQ0,sQuery(id+"F8.wireOp",EDGE,"E39.right")])]})]})});}
            var Q1;
            {var subQ0=sQuery(id+"F8.wireOp",EDGE,"E39.top");var subQ1=sQuery(id+"F0.wireOp",EDGE,"E1");var subQ2=sQuery(id+"F0.wireOp",EDGE,"E0");Q1=makeQuery(id+"F23.boolean.opBoolean","SPLIT",FACE,{"disambiguationData":[TD([makeQuery(id+"F23.opExtrude","SWEPT_FACE",FACE,{"disambiguationData":[OSD([sQuery(id+"F22.wireOp",EDGE,"E73")])]})])],"derivedFrom":makeQuery(id+"F11.boolean.opBoolean","MERGE",FACE,{"derivedFrom":[makeQuery(id+"F9.boolean.opBoolean","MERGE",FACE,{"derivedFrom":[makeQuery(id+"F7.boolean.opBoolean","MERGE",FACE,{"derivedFrom":[makeQuery(id+"F3.opExtrude","CAP_FACE",FACE,{"disambiguationData":[OSD([subQ2,subQ1,sQuery(id+"F0.wireOp",EDGE,"E2"),sQuery(id+"F2.wireOp",EDGE,"E6")])],"isStart":false}),makeQuery(id+"F7.opExtrude","SWEPT_FACE",FACE,{"disambiguationData":[OSD([subQ1]),TDD([makeQuery(id+"F6.imprint","IMPRINT",EDGE,{"derivedFrom":makeQuery(id+"F3.opExtrude","CAP_EDGE",EDGE,{"disambiguationData":[OSD([subQ1])],"isStart":false})})])]})]}),makeQuery(id+"F9.opExtrude","SWEPT_FACE",FACE,{"disambiguationData":[OSD([subQ0])]})]}),makeQuery(id+"F11.opExtrude","SWEPT_FACE",FACE,{"disambiguationData":[OSD([subQ2,subQ1,subQ0,sQuery(id+"F8.wireOp",EDGE,"E39.right")])]})]})});}
            var Q2;
            {var subQ0=sQuery(id+"F8.wireOp",EDGE,"E39.top");var subQ1=sQuery(id+"F0.wireOp",EDGE,"E1");var subQ2=sQuery(id+"F0.wireOp",EDGE,"E0");Q2=makeQuery(id+"F23.boolean.opBoolean","SPLIT",FACE,{"disambiguationData":[TD([makeQuery(id+"F23.opExtrude","SWEPT_FACE",FACE,{"disambiguationData":[OSD([sQuery(id+"F22.wireOp",EDGE,"E80")])]})])],"derivedFrom":makeQuery(id+"F11.boolean.opBoolean","MERGE",FACE,{"derivedFrom":[makeQuery(id+"F9.boolean.opBoolean","MERGE",FACE,{"derivedFrom":[makeQuery(id+"F7.boolean.opBoolean","MERGE",FACE,{"derivedFrom":[makeQuery(id+"F3.opExtrude","CAP_FACE",FACE,{"disambiguationData":[OSD([subQ2,subQ1,sQuery(id+"F0.wireOp",EDGE,"E2"),sQuery(id+"F2.wireOp",EDGE,"E6")])],"isStart":false}),makeQuery(id+"F7.opExtrude","SWEPT_FACE",FACE,{"disambiguationData":[OSD([subQ1]),TDD([makeQuery(id+"F6.imprint","IMPRINT",EDGE,{"derivedFrom":makeQuery(id+"F3.opExtrude","CAP_EDGE",EDGE,{"disambiguationData":[OSD([subQ1])],"isStart":false})})])]})]}),makeQuery(id+"F9.opExtrude","SWEPT_FACE",FACE,{"disambiguationData":[OSD([subQ0])]})]}),makeQuery(id+"F11.opExtrude","SWEPT_FACE",FACE,{"disambiguationData":[OSD([subQ2,subQ1,subQ0,sQuery(id+"F8.wireOp",EDGE,"E39.right")])]})]})});}
            var Q3;
            {var subQ0=sQuery(id+"F8.wireOp",EDGE,"E39.top");var subQ1=sQuery(id+"F0.wireOp",EDGE,"E1");var subQ2=sQuery(id+"F0.wireOp",EDGE,"E0");Q3=makeQuery(id+"F23.boolean.opBoolean","SPLIT",FACE,{"disambiguationData":[TD([makeQuery(id+"F23.opExtrude","SWEPT_FACE",FACE,{"disambiguationData":[OSD([sQuery(id+"F22.wireOp",EDGE,"E87")])]})])],"derivedFrom":makeQuery(id+"F11.boolean.opBoolean","MERGE",FACE,{"derivedFrom":[makeQuery(id+"F9.boolean.opBoolean","MERGE",FACE,{"derivedFrom":[makeQuery(id+"F7.boolean.opBoolean","MERGE",FACE,{"derivedFrom":[makeQuery(id+"F3.opExtrude","CAP_FACE",FACE,{"disambiguationData":[OSD([subQ2,subQ1,sQuery(id+"F0.wireOp",EDGE,"E2"),sQuery(id+"F2.wireOp",EDGE,"E6")])],"isStart":false}),makeQuery(id+"F7.opExtrude","SWEPT_FACE",FACE,{"disambiguationData":[OSD([subQ1]),TDD([makeQuery(id+"F6.imprint","IMPRINT",EDGE,{"derivedFrom":makeQuery(id+"F3.opExtrude","CAP_EDGE",EDGE,{"disambiguationData":[OSD([subQ1])],"isStart":false})})])]})]}),makeQuery(id+"F9.opExtrude","SWEPT_FACE",FACE,{"disambiguationData":[OSD([subQ0])]})]}),makeQuery(id+"F11.opExtrude","SWEPT_FACE",FACE,{"disambiguationData":[OSD([subQ2,subQ1,subQ0,sQuery(id+"F8.wireOp",EDGE,"E39.right")])]})]})});}
            extrude(context, id + "F24", {"entities" : qUnion([Q0, Q1, Q2, Q3]), "operationType" : NewBodyOperationType.REMOVE, "oppositeDirection" : true, "depth" : 20 * mm, "offsetDistance" : 25 * mm});
        }
        {
            var Q0;
            {var subQ0=sQuery(id+"F4.wireOp",EDGE,"E7");var subQ1=sQuery(id+"F0.wireOp",EDGE,"E1");var subQ2=sQuery(id+"F0.wireOp",EDGE,"E0");var subQ3=makeQuery(id+"F5.opExtrude","CAP_EDGE",EDGE,{"disambiguationData":[OSD([subQ0])],"isStart":false});Q0=makeQuery(id+"F11.boolean.opBoolean","MERGE",FACE,{"derivedFrom":[makeQuery(id+"F9.boolean.opBoolean","MERGE",FACE,{"derivedFrom":[makeQuery(id+"F7.boolean.opBoolean","MERGE",FACE,{"derivedFrom":[makeQuery(id+"F5.opExtrude","CAP_FACE",FACE,{"disambiguationData":[OSD([subQ2,subQ1,sQuery(id+"F0.wireOp",EDGE,"E2"),subQ0])],"isStart":false}),makeQuery(id+"F7.opExtrude","SWEPT_FACE",FACE,{"disambiguationData":[OSD([subQ1]),TDD([makeQuery(id+"F6.imprint","IMPRINT",EDGE,{"derivedFrom":makeQuery(id+"F5.opExtrude","CAP_EDGE",EDGE,{"disambiguationData":[OSD([subQ1])],"isStart":false})})])]})]}),makeQuery(id+"F9.opExtrude","SWEPT_FACE",FACE,{"disambiguationData":[OSD([subQ0]),TDD([makeQuery(id+"F8.imprint","IMPRINT",EDGE,{"disambiguationData":[TD([[makeQuery(id+"F8.imprint","INTERSECT",VERTEX,{"derivedFrom":[subQ3,sQuery(id+"F8.wireOp",EDGE,"E38")]}),-1.0]])],"derivedFrom":subQ3})])]})]}),makeQuery(id+"F11.opExtrude","SWEPT_FACE",FACE,{"disambiguationData":[OSD([subQ2,subQ1,subQ0])]})]});}
            var sketch = newSketch(context, id + "F25", { "sketchPlane" : qUnion([Q0])});
            skCircle(sketch, "E88", {"center": v(75, 75.73) * mm, "radius": 1.5 * mm});
            skCircle(sketch, "E89", {"center": v(75, 32.66) * mm, "radius": 1.5 * mm});
            skCircle(sketch, "E90", {"center": v(13.46, -5.8) * mm, "radius": 1.5 * mm});
            skCircle(sketch, "E91", {"center": v(36.54, -5.8) * mm, "radius": 1.5 * mm});
            skSolve(sketch);
        }
        {
            var Q0;
            Q0=makeQuery(id+"F25.imprint","IMPRINT",FACE,{"disambiguationData":[TD([[makeQuery(id+"F25.imprint","IMPRINT",EDGE,{"derivedFrom":sQuery(id+"F25.wireOp",EDGE,"E89")}),1.0]])]});
            var Q1;
            Q1=makeQuery(id+"F25.imprint","IMPRINT",FACE,{"disambiguationData":[TD([[makeQuery(id+"F25.imprint","IMPRINT",EDGE,{"derivedFrom":sQuery(id+"F25.wireOp",EDGE,"E88")}),1.0]])]});
            var Q2;
            Q2=makeQuery(id+"F25.imprint","IMPRINT",FACE,{"disambiguationData":[TD([[makeQuery(id+"F25.imprint","IMPRINT",EDGE,{"derivedFrom":sQuery(id+"F25.wireOp",EDGE,"E91")}),1.0]])]});
            var Q3;
            Q3=makeQuery(id+"F25.imprint","IMPRINT",FACE,{"disambiguationData":[TD([[makeQuery(id+"F25.imprint","IMPRINT",EDGE,{"derivedFrom":sQuery(id+"F25.wireOp",EDGE,"E90")}),1.0]])]});
            extrude(context, id + "F26", {"entities" : qUnion([Q0, Q1, Q2, Q3]), "operationType" : NewBodyOperationType.REMOVE, "oppositeDirection" : true, "depth" : 20 * mm, "offsetDistance" : 25 * mm});
        }
        {
            var Q0;
            Q0=makeQuery(id+"F1.opExtrude","CAP_FACE",FACE,{"disambiguationData":[OSD([sQuery(id+"F0.wireOp",EDGE,"E0"),sQuery(id+"F0.wireOp",EDGE,"E1"),sQuery(id+"F0.wireOp",EDGE,"E2"),sQuery(id+"F0.wireOp",EDGE,"E3"),sQuery(id+"F0.wireOp",EDGE,"E4"),sQuery(id+"F0.wireOp",EDGE,"E5")])],"isStart":false});
            var sketch = newSketch(context, id + "F27", { "sketchPlane" : qUnion([Q0])});
            skLineSegment(sketch, "E92", {"start": v(-35.46, 49.2) * mm, "end": v(-33.73, 46.2) * mm});
            skLineSegment(sketch, "E93", {"start": v(-33.73, 46.2) * mm, "end": v(-30.27, 46.2) * mm});
            skLineSegment(sketch, "E94", {"start": v(-30.27, 46.2) * mm, "end": v(-28.54, 49.2) * mm});
            skLineSegment(sketch, "E95", {"start": v(-28.54, 49.2) * mm, "end": v(-30.27, 52.2) * mm});
            skLineSegment(sketch, "E96", {"start": v(-30.27, 52.2) * mm, "end": v(-33.73, 52.2) * mm});
            skLineSegment(sketch, "E97", {"start": v(-33.73, 52.2) * mm, "end": v(-35.46, 49.2) * mm});
            skCircle(sketch, "E98", {"center": v(-32, 49.2) * mm, "radius": 1.5 * mm});
            skLineSegment(sketch, "E99", {"start": v(-16.21, 49.2) * mm, "end": v(-14.48, 46.2) * mm});
            skLineSegment(sketch, "E100", {"start": v(-14.48, 46.2) * mm, "end": v(-11.02, 46.2) * mm});
            skLineSegment(sketch, "E101", {"start": v(-11.02, 46.2) * mm, "end": v(-9.29, 49.2) * mm});
            skLineSegment(sketch, "E102", {"start": v(-9.29, 49.2) * mm, "end": v(-11.02, 52.2) * mm});
            skLineSegment(sketch, "E103", {"start": v(-11.02, 52.2) * mm, "end": v(-14.48, 52.2) * mm});
            skLineSegment(sketch, "E104", {"start": v(-14.48, 52.2) * mm, "end": v(-16.21, 49.2) * mm});
            skCircle(sketch, "E105", {"center": v(-12.75, 49.2) * mm, "radius": 1.5 * mm});
            skSolve(sketch);
        }
        {
            var Q0;
            Q0=makeQuery(id+"F27.imprint","IMPRINT",FACE,{"disambiguationData":[TD([[makeQuery(id+"F27.imprint","IMPRINT",EDGE,{"derivedFrom":sQuery(id+"F27.wireOp",EDGE,"E92")}),1.0]])]});
            var Q1;
            Q1=makeQuery(id+"F27.imprint","IMPRINT",FACE,{"disambiguationData":[TD([[makeQuery(id+"F27.imprint","IMPRINT",EDGE,{"derivedFrom":sQuery(id+"F27.wireOp",EDGE,"E99")}),1.0]])]});
            extrude(context, id + "F28", {"entities" : qUnion([Q0, Q1]), "operationType" : NewBodyOperationType.REMOVE, "oppositeDirection" : true, "depth" : 3 * mm, "offsetDistance" : 25 * mm});
        }
        {
            var Q0;
            Q0=makeQuery(id+"F28.boolean.opBoolean","SPLIT",FACE,{"disambiguationData":[TD([makeQuery(id+"F28.opExtrude","SWEPT_FACE",FACE,{"disambiguationData":[OSD([sQuery(id+"F27.wireOp",EDGE,"E98")])]})])],"derivedFrom":makeQuery(id+"F1.opExtrude","CAP_FACE",FACE,{"disambiguationData":[OSD([sQuery(id+"F0.wireOp",EDGE,"E0"),sQuery(id+"F0.wireOp",EDGE,"E1"),sQuery(id+"F0.wireOp",EDGE,"E2"),sQuery(id+"F0.wireOp",EDGE,"E3"),sQuery(id+"F0.wireOp",EDGE,"E4"),sQuery(id+"F0.wireOp",EDGE,"E5")])],"isStart":false})});
            var Q1;
            Q1=makeQuery(id+"F28.boolean.opBoolean","SPLIT",FACE,{"disambiguationData":[TD([makeQuery(id+"F28.opExtrude","SWEPT_FACE",FACE,{"disambiguationData":[OSD([sQuery(id+"F27.wireOp",EDGE,"E105")])]})])],"derivedFrom":makeQuery(id+"F1.opExtrude","CAP_FACE",FACE,{"disambiguationData":[OSD([sQuery(id+"F0.wireOp",EDGE,"E0"),sQuery(id+"F0.wireOp",EDGE,"E1"),sQuery(id+"F0.wireOp",EDGE,"E2"),sQuery(id+"F0.wireOp",EDGE,"E3"),sQuery(id+"F0.wireOp",EDGE,"E4"),sQuery(id+"F0.wireOp",EDGE,"E5")])],"isStart":false})});
            extrude(context, id + "F29", {"entities" : qUnion([Q0, Q1]), "operationType" : NewBodyOperationType.REMOVE, "oppositeDirection" : true, "depth" : 10 * mm, "offsetDistance" : 25 * mm});
        }
        {
            var Q0;
            Q0=makeQuery(id+"F1.opExtrude","CAP_FACE",FACE,{"disambiguationData":[OSD([sQuery(id+"F0.wireOp",EDGE,"E0"),sQuery(id+"F0.wireOp",EDGE,"E1"),sQuery(id+"F0.wireOp",EDGE,"E2"),sQuery(id+"F0.wireOp",EDGE,"E3"),sQuery(id+"F0.wireOp",EDGE,"E4"),sQuery(id+"F0.wireOp",EDGE,"E5")])],"isStart":true});
            var sketch = newSketch(context, id + "F30", { "sketchPlane" : qUnion([Q0])});
            skCircle(sketch, "E106", {"center": v(32, 49.2) * mm, "radius": 1.5 * mm});
            skCircle(sketch, "E107", {"center": v(12.75, 49.2) * mm, "radius": 1.5 * mm});
            skSolve(sketch);
        }
        {
            var Q0;
            Q0=makeQuery(id+"F30.imprint","IMPRINT",FACE,{"disambiguationData":[TD([[makeQuery(id+"F30.imprint","IMPRINT",EDGE,{"derivedFrom":sQuery(id+"F30.wireOp",EDGE,"E106")}),1.0]])]});
            var Q1;
            Q1=makeQuery(id+"F30.imprint","IMPRINT",FACE,{"disambiguationData":[TD([[makeQuery(id+"F30.imprint","IMPRINT",EDGE,{"derivedFrom":sQuery(id+"F30.wireOp",EDGE,"E107")}),1.0]])]});
            extrude(context, id + "F31", {"entities" : qUnion([Q0, Q1]), "operationType" : NewBodyOperationType.REMOVE, "oppositeDirection" : true, "depth" : 10 * mm, "offsetDistance" : 25 * mm});
        }
    });
